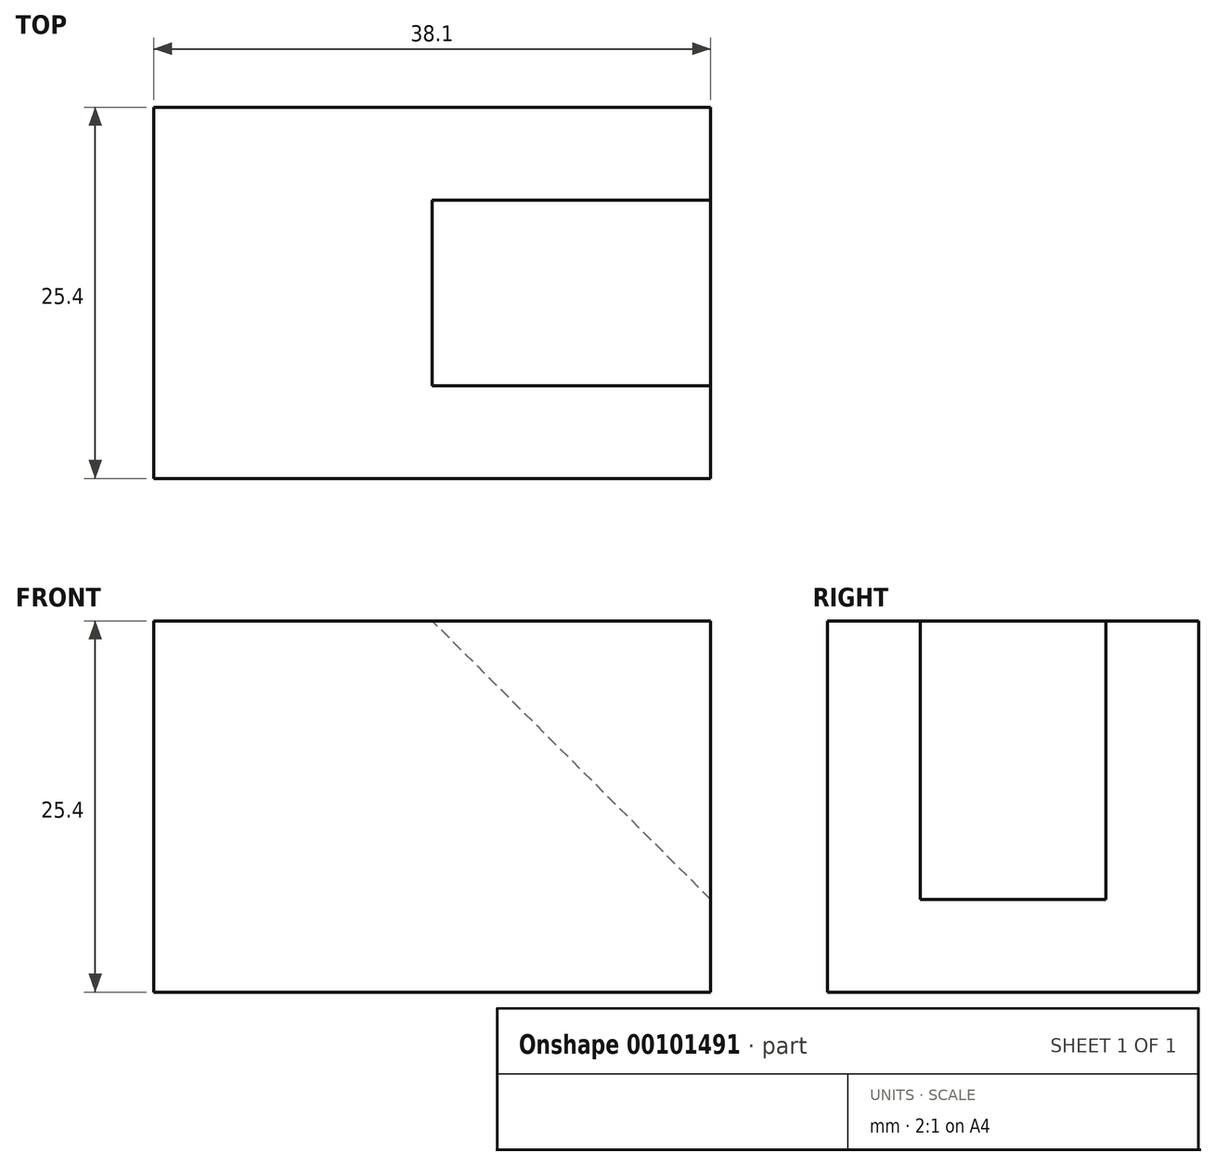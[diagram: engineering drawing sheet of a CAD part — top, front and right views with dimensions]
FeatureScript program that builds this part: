
annotation { "Feature Type Name" : "Feature", "Feature Type Description" : "" }
export const myFeature = defineFeature(function(context is Context, id is Id, definition is map)
    precondition{}
    {
        {
            var Q0;
            Q0=qCreatedBy(makeId("Front.planeOp"),FACE);
            var sketch = newSketch(context, id + "F0", { "sketchPlane" : qUnion([Q0])});
            skLineSegment(sketch, "E0.bottom", {"start": v(0, 0) * mm, "end": v(38.1, 0) * mm});
            skLineSegment(sketch, "E0.top", {"start": v(0, 25.4) * mm, "end": v(38.1, 25.4) * mm});
            skLineSegment(sketch, "E0.left", {"start": v(0, 0) * mm, "end": v(0, 25.4) * mm});
            skLineSegment(sketch, "E0.right", {"start": v(38.1, 0) * mm, "end": v(38.1, 25.4) * mm});
            skSolve(sketch);
        }
        {
            var Q0;
            Q0=makeQuery(id+"F0.imprint","IMPRINT",FACE,{"disambiguationData":[TD([[makeQuery(id+"F0.imprint","IMPRINT",EDGE,{"derivedFrom":sQuery(id+"F0.wireOp",EDGE,"E0.bottom")}),1.0]])]});
            extrude(context, id + "F1", {"entities" : qUnion([Q0]), "depth" : 25.4 * mm});
        }
        {
            var Q0;
            Q0=makeQuery(id+"F1.opExtrude","CAP_FACE",FACE,{"disambiguationData":[OSD([sQuery(id+"F0.wireOp",EDGE,"E0.bottom"),sQuery(id+"F0.wireOp",EDGE,"E0.top"),sQuery(id+"F0.wireOp",EDGE,"E0.left"),sQuery(id+"F0.wireOp",EDGE,"E0.right")])],"isStart":false});
            var sketch = newSketch(context, id + "F2", { "sketchPlane" : qUnion([Q0])});
            skLineSegment(sketch, "E1", {"start": v(38.1, 6.35) * mm, "end": v(19.05, 25.4) * mm});
            skSolve(sketch);
        }
        {
            var Q0;
            {var subQ0=sQuery(id+"F2.wireOp",EDGE,"E1");Q0=makeQuery(id+"F2.imprint","IMPRINT",FACE,{"disambiguationData":[TD([[makeQuery(id+"F2.imprint","IMPRINT",EDGE,{"derivedFrom":subQ0}),-1.0]])]});}
            extrude(context, id + "F3", {"entities" : qUnion([Q0]), "operationType" : NewBodyOperationType.REMOVE, "oppositeDirection" : true, "depth" : 19.05 * mm, "hasSecondDirection" : true, "secondDirectionOppositeDirection" : true, "secondDirectionDepth" : 6.35 * mm});
        }
    });
